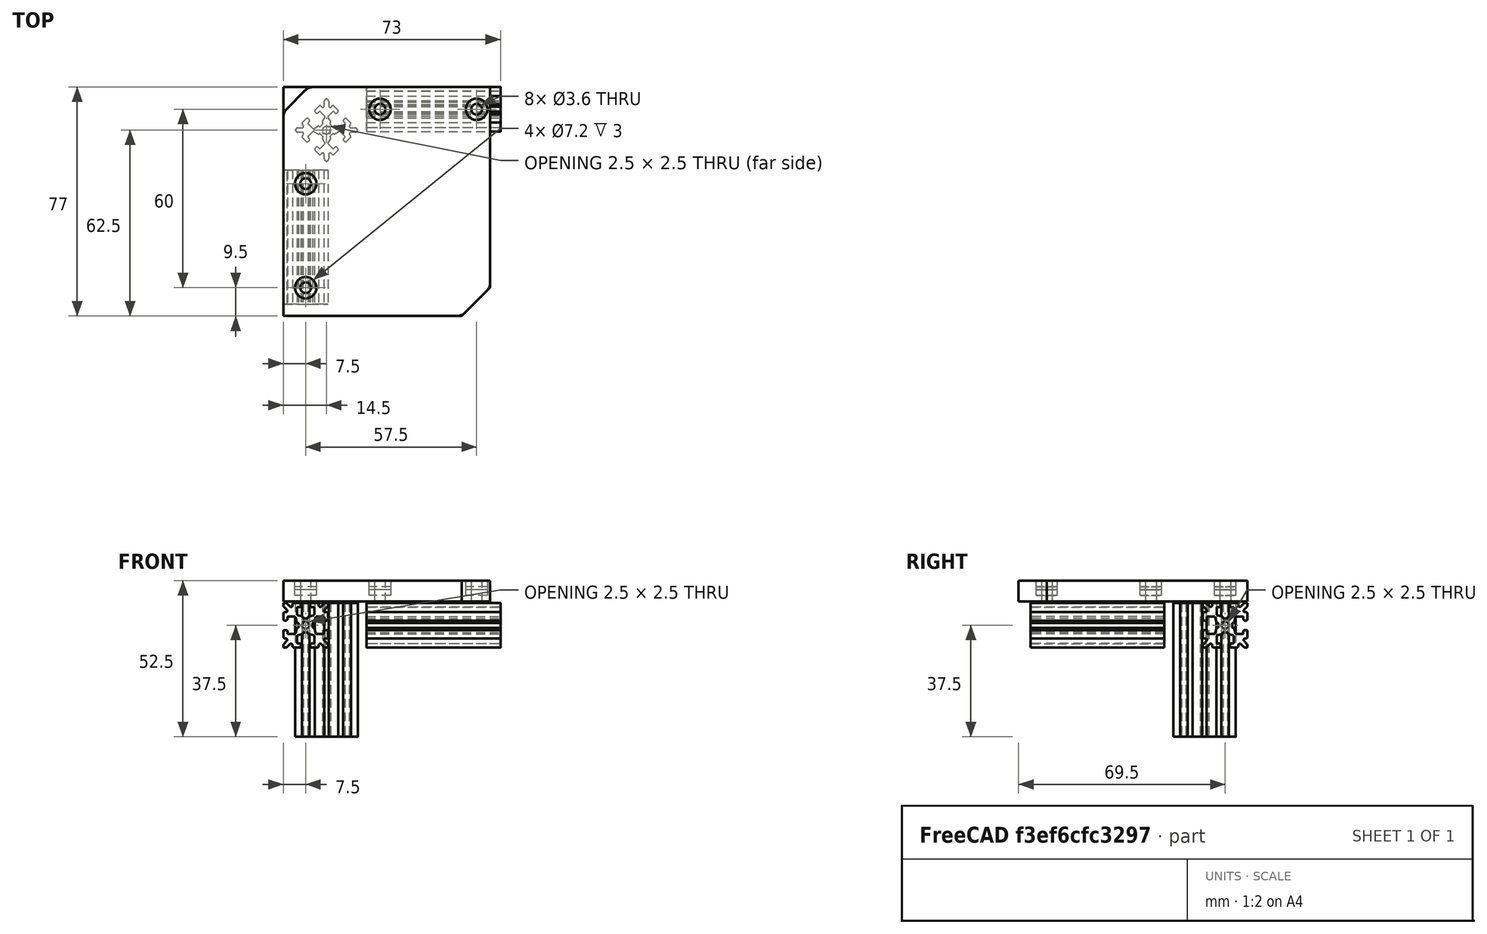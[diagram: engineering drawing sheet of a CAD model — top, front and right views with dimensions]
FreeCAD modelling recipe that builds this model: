
FCSTD DOCUMENT  (FreeCAD 0.15R4671 (Git))
Label: TopCornerCapBlank
License: All rights reserved
LicenseURL: http://en.wikipedia.org/wiki/All_rights_reserved
objects: Sketcher::SketchObject×3, Part::Feature×3, PartDesign::Pocket×2, PartDesign::Fillet×2, PartDesign::Pad×1, Mesh::Feature×1
note: 14 computed .brp shape members not serialized (recipe doc carries the construction recipe); baked Part::Feature solids carry a one-line shape summary decoded from their .brp

FEATURE [Sketcher::SketchObject] Sketch
  Placement = pos=(0,0,2) rot=(0,0,1;0rad)
  sketch-geometry (9):
    g0: LineSegment StartX=-7.5 StartY=7.5 StartZ=0 EndX=62.0538 EndY=7.5 EndZ=0
    g1: LineSegment StartX=62.0538 StartY=7.5 StartZ=0 EndX=62.0538 EndY=-59.9462 EndZ=0
    g2: LineSegment StartX=62.0538 StartY=-59.9462 StartZ=0 EndX=52.5 EndY=-69.5 EndZ=0
    g3: LineSegment StartX=52.5 StartY=-69.5 StartZ=0 EndX=-7.5 EndY=-69.5 EndZ=0
    g4: LineSegment StartX=-7.5 StartY=-69.5 StartZ=0 EndX=-7.5 EndY=7.5 EndZ=0
    g5: Circle CenterX=25 CenterY=0 CenterZ=0 NormalX=0 NormalY=0 NormalZ=1 Radius=1.8
    g6: Circle CenterX=57.5 CenterY=0 CenterZ=0 NormalX=0 NormalY=0 NormalZ=1 Radius=1.8
    g7: Circle CenterX=0 CenterY=-25 CenterZ=0 NormalX=0 NormalY=0 NormalZ=1 Radius=1.8
    g8: Circle CenterX=0 CenterY=-60 CenterZ=0 NormalX=0 NormalY=0 NormalZ=1 Radius=1.8
  constraints (16):
    c: Coincident(g0,g1)
    c: Coincident(g1,g2)
    c: Coincident(g2,g3)
    c: Coincident(g3,g4)
    c: Coincident(g4,g0)
    c: Horizontal(g3)
    c: Horizontal(g0)
    c: Vertical(g1)
    c: Vertical(g4)
    c: Angle(g2,g-2) = 0.785398
    c: DistanceX(g0) = -7.5
    c: DistanceY(g0) = 7.5
    c: Radius(g5) = 1.8
    c: Radius(g6) = 1.8
    c: Radius(g7) = 1.8
    c: Radius(g8) = 1.8
FEATURE [Part::Feature] Part__Feature  label="OB1515_45mm001"
  Placement = pos=(0,-20.5,-6) rot=(1,0,0;1.5708rad)
  shape: bbox 15 x 45 x 15 mm, 158 faces (baked)
FEATURE [Part::Feature] Part__Feature001  label="OB1515_45mm002"
  Placement = pos=(20.5,0,-6) rot=(0.57735,0.57735,0.57735;2.0944rad)
  shape: bbox 45 x 15 x 15 mm, 158 faces (baked)
FEATURE [Part::Feature] Part__Feature002  label="OB1515_45mm"
  Placement = pos=(7,-7,-43.5) rot=(0,0,1;0.785398rad)
  shape: bbox 21.01 x 21.01 x 45 mm, 158 faces (baked)
FEATURE [PartDesign::Pad] Pad
  Length = 7
  Length2 = 100
  Placement = pos=(0,0,2) rot=(0,0,1;0rad)
  Sketch = -> Sketch
  Type = 0
FEATURE [Sketcher::SketchObject] Sketch001
  Placement = pos=(0,0,9) rot=(0,0,1;0rad)
  Support = -> Pad [Face11]
  sketch-geometry (4):
    g0: Circle CenterX=57.5 CenterY=0 CenterZ=0 NormalX=0 NormalY=0 NormalZ=1 Radius=3.6
    g1: Circle CenterX=25 CenterY=0 CenterZ=0 NormalX=0 NormalY=0 NormalZ=1 Radius=3.6
    g2: Circle CenterX=0 CenterY=-25 CenterZ=0 NormalX=0 NormalY=0 NormalZ=1 Radius=3.6
    g3: Circle CenterX=0 CenterY=-60 CenterZ=0 NormalX=0 NormalY=0 NormalZ=1 Radius=3.6
  constraints (4):
    c: Radius(g0) = 3.6
    c: Radius(g1) = 3.6
    c: Radius(g2) = 3.6
    c: Radius(g3) = 3.6
FEATURE [PartDesign::Pocket] Pocket
  Length = 3
  Placement = pos=(0,0,2) rot=(0,0,1;0rad)
  Sketch = -> Sketch001
  Type = 0
FEATURE [Mesh::Feature] temp
FEATURE [Sketcher::SketchObject] Sketch002
  Placement = pos=(0,0,9) rot=(0,0,1;0rad)
  Support = -> Pocket [Face5]
  sketch-geometry (5):
    g0: LineSegment StartX=-8.5 StartY=-1 StartZ=0 EndX=-7.5 EndY=-1 EndZ=0
    g1: LineSegment StartX=-7.5 StartY=-1 StartZ=0 EndX=1 EndY=7.5 EndZ=0
    g2: LineSegment StartX=1 StartY=7.5 StartZ=0 EndX=1 EndY=8.5 EndZ=0
    g3: LineSegment StartX=1 StartY=8.5 StartZ=0 EndX=-8.5 EndY=8.5 EndZ=0
    g4: LineSegment StartX=-8.5 StartY=8.5 StartZ=0 EndX=-8.5 EndY=-1 EndZ=0
  constraints (5):
    c: Coincident(g0,g1)
    c: Coincident(g1,g2)
    c: Coincident(g2,g3)
    c: Coincident(g3,g4)
    c: Coincident(g4,g0)
FEATURE [PartDesign::Pocket] Pocket001
  Length = 5
  Placement = pos=(0,0,2) rot=(0,0,1;0rad)
  Sketch = -> Sketch002
  Type = 1
FEATURE [PartDesign::Fillet] Fillet
  Base = -> Pocket001 [Edge4,Edge24]
  Placement = pos=(0,0,2) rot=(0,0,1;0rad)
  Radius = 4
FEATURE [PartDesign::Fillet] Fillet001
  Base = -> Fillet [Edge30,Edge18]
  Placement = pos=(0,0,2) rot=(0,0,1;0rad)
  Radius = 4
